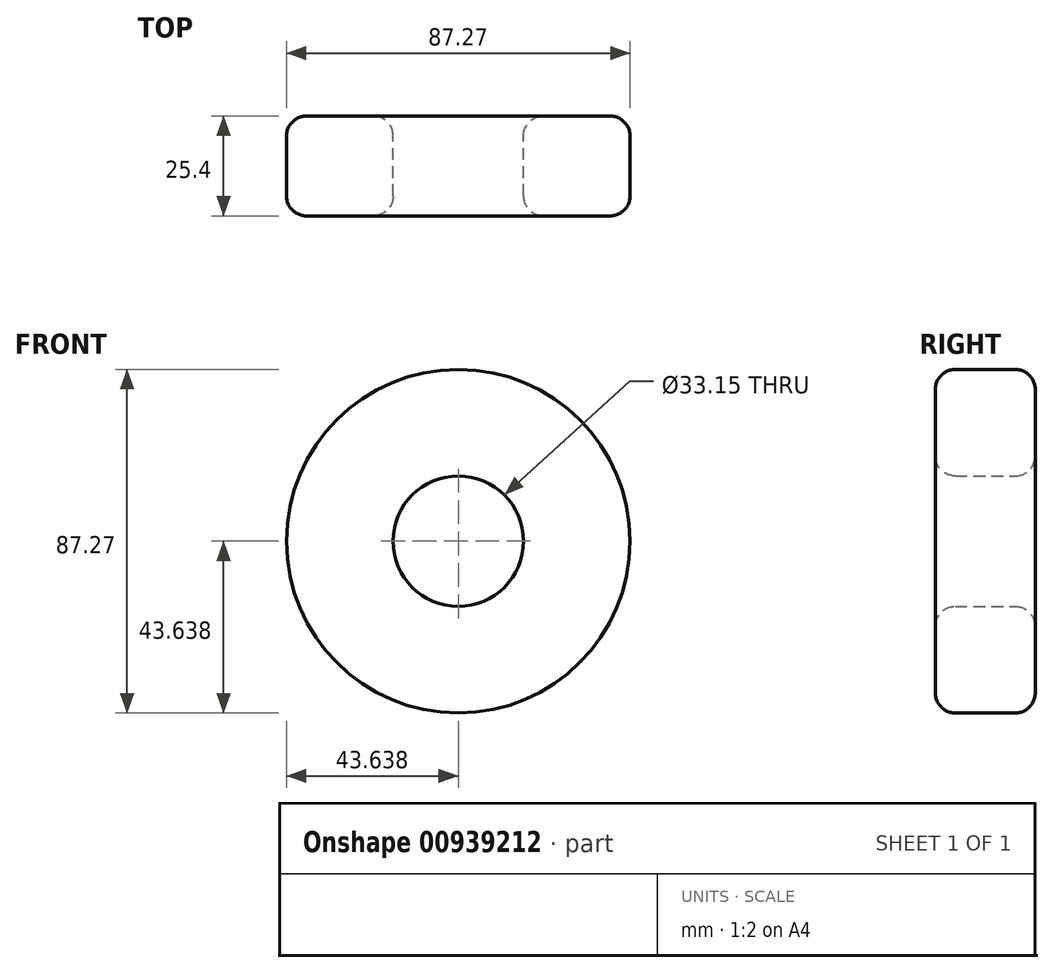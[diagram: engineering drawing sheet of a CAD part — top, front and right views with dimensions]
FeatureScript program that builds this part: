
annotation { "Feature Type Name" : "Feature", "Feature Type Description" : "" }
export const myFeature = defineFeature(function(context is Context, id is Id, definition is map)
    precondition{}
    {
        {
            var Q0;
            Q0=qCreatedBy(makeId("Front.planeOp"),FACE);
            var sketch = newSketch(context, id + "F0", { "sketchPlane" : qUnion([Q0])});
            skCircle(sketch, "E0", {"center": v(-89.95, 22.56) * mm, "radius": 43.64 * mm});
            skCircle(sketch, "E1", {"center": v(-89.95, 22.56) * mm, "radius": 16.58 * mm});
            skSolve(sketch);
        }
        {
            var Q0;
            Q0 = qSketchRegion(id + "F0", true);
            extrude(context, id + "F1", {"entities" : qUnion([Q0]), "depth" : 25.4 * mm, "offsetDistance" : 25.4 * mm});
        }
        {
            var Q0;
            Q0=makeQuery(id+"F1.opExtrude","CAP_FACE",FACE,{"disambiguationData":[OSD([sQuery(id+"F0.wireOp",EDGE,"E0"),sQuery(id+"F0.wireOp",EDGE,"E1")])],"isStart":true});
            var Q1;
            Q1=makeQuery(id+"F1.opExtrude","CAP_FACE",FACE,{"disambiguationData":[OSD([sQuery(id+"F0.wireOp",EDGE,"E0"),sQuery(id+"F0.wireOp",EDGE,"E1")])],"isStart":false});
            fillet(context, id + "F2", {"entities" : qUnion([Q0, Q1]), "radius" : 5.08 * mm, "tangentPropagation" : true, "allowEdgeOverflow" : false});
        }
    });
